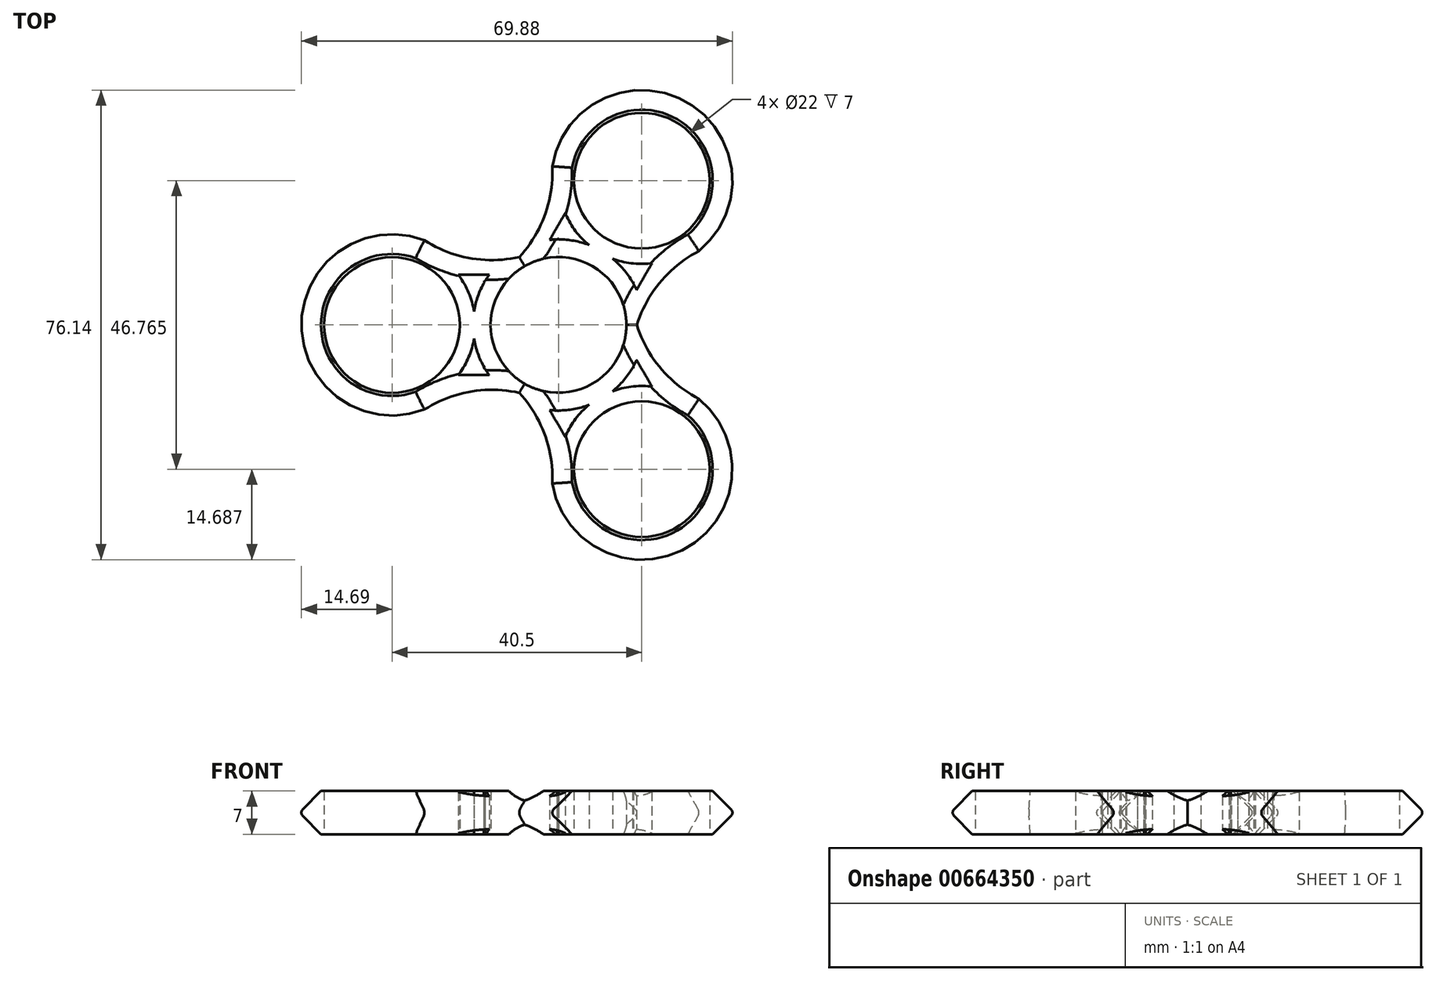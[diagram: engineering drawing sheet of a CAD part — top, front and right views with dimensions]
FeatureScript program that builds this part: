
annotation { "Feature Type Name" : "Feature", "Feature Type Description" : "" }
export const myFeature = defineFeature(function(context is Context, id is Id, definition is map)
    precondition{}
    {
        {
            var Q0;
            Q0=qCreatedBy(makeId("Front.planeOp"),FACE);
            var sketch = newSketch(context, id + "F0", { "sketchPlane" : qUnion([Q0])});
            skLineSegment(sketch, "E0", {"start": v(0, 0) * mm, "end": v(0, 6.18) * mm});
            skSolve(sketch);
        }
        {
            var Q0;
            Q0=qCreatedBy(makeId("Top.planeOp"),FACE);
            var sketch = newSketch(context, id + "F1", { "sketchPlane" : qUnion([Q0])});
            skArc(sketch, "E1", {"start": v(0, 11) * mm, "mid": v(-11, 0) * mm, "end": v(0, -11) * mm});
            skLineSegment(sketch, "E2", {"start": v(0, 56.07) * mm, "end": v(0, 11) * mm, "construction": true});
            skLineSegment(sketch, "E3", {"start": v(-42, 56.32) * mm, "end": v(-42, -55.95) * mm, "construction": true});
            skArc(sketch, "E4", {"start": v(-21.61, 14) * mm, "mid": v(-42, 0) * mm, "end": v(-21.61, -14) * mm});
            skLineSegment(sketch, "E5", {"start": v(0, 14) * mm, "end": v(0, 11) * mm});
            skLineSegment(sketch, "E6.trimOffspring", {"start": v(0, -11) * mm, "end": v(0, -55.82) * mm, "construction": true});
            skLineSegment(sketch, "E7.trimOffspring", {"start": v(0, -11) * mm, "end": v(0, -14) * mm});
            skCircle(sketch, "E8", {"center": v(-27, 0) * mm, "radius": 11 * mm});
            skArc(sketch, "E9", {"start": v(-21.61, 14) * mm, "mid": v(-10.8, 10.83) * mm, "end": v(0, 14) * mm});
            skArc(sketch, "E10", {"start": v(0, -14) * mm, "mid": v(-10.8, -10.83) * mm, "end": v(-21.61, -14) * mm});
            skArc(sketch, "E11", {"start": v(-16.24, -8.13) * mm, "mid": v(-14.6, -5.32) * mm, "end": v(-13.7, -2.2) * mm});
            skArc(sketch, "E12", {"start": v(-13.7, -2.2) * mm, "mid": v(-12.82, -5.3) * mm, "end": v(-11.24, -8.13) * mm});
            skLineSegment(sketch, "E13", {"start": v(-16.24, 8.13) * mm, "end": v(-11.24, 8.13) * mm});
            skLineSegment(sketch, "E14", {"start": v(-16.24, -8.13) * mm, "end": v(-11.24, -8.13) * mm});
            skArc(sketch, "E15.trimOffspring", {"start": v(-13.7, 2.2) * mm, "mid": v(-14.6, 5.32) * mm, "end": v(-16.24, 8.13) * mm});
            skArc(sketch, "E16.trimOffspring", {"start": v(-11.24, 8.13) * mm, "mid": v(-12.82, 5.3) * mm, "end": v(-13.7, 2.2) * mm});
            skArc(sketch, "E17.trimOffspring", {"start": v(0, 13.87) * mm, "mid": v(-0.1, 13.87) * mm, "end": v(-0.2, 13.87) * mm});
            skArc(sketch, "E18.trimOffspring", {"start": v(-0.2, -13.87) * mm, "mid": v(-0.1, -13.87) * mm, "end": v(0, -13.87) * mm});
            skSolve(sketch);
        }
        {
            var Q0;
            Q0=qSketchRegion(id+"F1",true);
            extrude(context, id + "F2", {"entities" : qUnion([Q0]), "depth" : 7 * mm, "offsetDistance" : 25 * mm});
        }
        {
            var Q0;
            Q0=makeQuery(id+"F2.opExtrude","SWEPT_BODY",BODY,{"disambiguationData":[OSD([sQuery(id+"F1.wireOp",EDGE,"E1"),sQuery(id+"F1.wireOp",EDGE,"E4"),sQuery(id+"F1.wireOp",EDGE,"FDauGuLe-8Zff-q5YO-oCp6-tykGBjxohg7e"),sQuery(id+"F1.wireOp",EDGE,"jIsLD8pJ-Ysfo-LJuf-yR93-SOJIJmbdSe7O"),sQuery(id+"F1.wireOp",EDGE,"E5"),sQuery(id+"F1.wireOp",EDGE,"E7.trimOffspring"),sQuery(id+"F1.wireOp",EDGE,"E8")])]});
            var Q1;
            Q1=sQuery(id+"F0.wireOp",EDGE,"E0");
            circularPattern(context, id + "F3", {"operationType" : NewBodyOperationType.ADD, "entities" : qUnion([Q0]), "axis" : qUnion([Q1]), "angle" : 240 * degree, "instanceCount" : 3, "equalSpace" : true});
        }
        {
            var Q0;
            {var subQ0=sQuery(id+"F1.wireOp",EDGE,"E10");var subQ2=sQuery(id+"F1.wireOp",EDGE,"E4");Q0=makeQuery(id+"F3.boolean.opBoolean","SPLIT",EDGE,{"disambiguationData":[TD([makeQuery(id+"F2.opExtrude","SWEPT_FACE",FACE,{"disambiguationData":[OSD([subQ2])]})])],"derivedFrom":makeQuery(id+"F2.opExtrude","CAP_EDGE",EDGE,{"disambiguationData":[OSD([subQ0])],"isStart":false})});}
            var Q1;
            {var subQ1=sQuery(id+"F1.wireOp",EDGE,"E10");var subQ2=sQuery(id+"F1.wireOp",EDGE,"E9");Q1=makeQuery(id+"F3.boolean.opBoolean","SPLIT",EDGE,{"disambiguationData":[TD([makeQuery(id+"F2.opExtrude","SWEPT_FACE",FACE,{"disambiguationData":[OSD([subQ1])]})])],"derivedFrom":makeQuery(id+"F3.opPattern","COPY",EDGE,{"derivedFrom":makeQuery(id+"F2.opExtrude","CAP_EDGE",EDGE,{"disambiguationData":[OSD([subQ2])],"isStart":false}),"instanceName":"1"})});}
            var Q2;
            Q2=makeQuery(id+"F3.opPattern","COPY",EDGE,{"derivedFrom":makeQuery(id+"F2.opExtrude","CAP_EDGE",EDGE,{"disambiguationData":[OSD([sQuery(id+"F1.wireOp",EDGE,"E4")])],"isStart":false}),"instanceName":"1"});
            var Q3;
            {var subQ0=sQuery(id+"F1.wireOp",EDGE,"E10");var subQ1=sQuery(id+"F1.wireOp",EDGE,"E4");Q3=makeQuery(id+"F3.boolean.opBoolean","SPLIT",EDGE,{"disambiguationData":[TD([makeQuery(id+"F3.opPattern","COPY",FACE,{"derivedFrom":makeQuery(id+"F2.opExtrude","SWEPT_FACE",FACE,{"disambiguationData":[OSD([subQ1])]}),"instanceName":"1"})])],"derivedFrom":makeQuery(id+"F3.opPattern","COPY",EDGE,{"derivedFrom":makeQuery(id+"F2.opExtrude","CAP_EDGE",EDGE,{"disambiguationData":[OSD([subQ0])],"isStart":false}),"instanceName":"1"})});}
            var Q4;
            {var subQ0=sQuery(id+"F1.wireOp",EDGE,"E10");var subQ1=sQuery(id+"F1.wireOp",EDGE,"E9");Q4=makeQuery(id+"F3.boolean.opBoolean","SPLIT",EDGE,{"disambiguationData":[TD([makeQuery(id+"F3.opPattern","COPY",FACE,{"derivedFrom":makeQuery(id+"F2.opExtrude","SWEPT_FACE",FACE,{"disambiguationData":[OSD([subQ0])]}),"instanceName":"1"})])],"derivedFrom":makeQuery(id+"F3.opPattern","COPY",EDGE,{"derivedFrom":makeQuery(id+"F2.opExtrude","CAP_EDGE",EDGE,{"disambiguationData":[OSD([subQ1])],"isStart":false}),"instanceName":"2"})});}
            var Q5;
            Q5=makeQuery(id+"F3.opPattern","COPY",EDGE,{"derivedFrom":makeQuery(id+"F2.opExtrude","CAP_EDGE",EDGE,{"disambiguationData":[OSD([sQuery(id+"F1.wireOp",EDGE,"E4")])],"isStart":false}),"instanceName":"2"});
            var Q6;
            {var subQ0=sQuery(id+"F1.wireOp",EDGE,"E10");var subQ1=sQuery(id+"F1.wireOp",EDGE,"E9");Q6=makeQuery(id+"F3.boolean.opBoolean","SPLIT",EDGE,{"disambiguationData":[TD([makeQuery(id+"F2.opExtrude","SWEPT_FACE",FACE,{"disambiguationData":[OSD([subQ1])]})])],"derivedFrom":makeQuery(id+"F3.opPattern","COPY",EDGE,{"derivedFrom":makeQuery(id+"F2.opExtrude","CAP_EDGE",EDGE,{"disambiguationData":[OSD([subQ0])],"isStart":false}),"instanceName":"2"})});}
            var Q7;
            {var subQ1=sQuery(id+"F1.wireOp",EDGE,"E9");var subQ2=sQuery(id+"F1.wireOp",EDGE,"E4");Q7=makeQuery(id+"F3.boolean.opBoolean","SPLIT",EDGE,{"disambiguationData":[TD([makeQuery(id+"F2.opExtrude","SWEPT_FACE",FACE,{"disambiguationData":[OSD([subQ2])]})])],"derivedFrom":makeQuery(id+"F2.opExtrude","CAP_EDGE",EDGE,{"disambiguationData":[OSD([subQ1])],"isStart":false})});}
            var Q8;
            Q8=makeQuery(id+"F2.opExtrude","CAP_EDGE",EDGE,{"disambiguationData":[OSD([sQuery(id+"F1.wireOp",EDGE,"E4")])],"isStart":false});
            var Q9;
            Q9=makeQuery(id+"F2.opExtrude","CAP_EDGE",EDGE,{"disambiguationData":[OSD([sQuery(id+"F1.wireOp",EDGE,"E4")])],"isStart":true});
            var Q10;
            {var subQ0=sQuery(id+"F1.wireOp",EDGE,"E10");var subQ2=sQuery(id+"F1.wireOp",EDGE,"E4");Q10=makeQuery(id+"F3.boolean.opBoolean","SPLIT",EDGE,{"disambiguationData":[TD([makeQuery(id+"F2.opExtrude","SWEPT_FACE",FACE,{"disambiguationData":[OSD([subQ2])]})])],"derivedFrom":makeQuery(id+"F2.opExtrude","CAP_EDGE",EDGE,{"disambiguationData":[OSD([subQ0])],"isStart":true})});}
            var Q11;
            {var subQ1=sQuery(id+"F1.wireOp",EDGE,"E10");var subQ2=sQuery(id+"F1.wireOp",EDGE,"E9");Q11=makeQuery(id+"F3.boolean.opBoolean","SPLIT",EDGE,{"disambiguationData":[TD([makeQuery(id+"F2.opExtrude","SWEPT_FACE",FACE,{"disambiguationData":[OSD([subQ1])]})])],"derivedFrom":makeQuery(id+"F3.opPattern","COPY",EDGE,{"derivedFrom":makeQuery(id+"F2.opExtrude","CAP_EDGE",EDGE,{"disambiguationData":[OSD([subQ2])],"isStart":true}),"instanceName":"1"})});}
            var Q12;
            Q12=makeQuery(id+"F3.opPattern","COPY",EDGE,{"derivedFrom":makeQuery(id+"F2.opExtrude","CAP_EDGE",EDGE,{"disambiguationData":[OSD([sQuery(id+"F1.wireOp",EDGE,"E4")])],"isStart":true}),"instanceName":"1"});
            var Q13;
            {var subQ0=sQuery(id+"F1.wireOp",EDGE,"E10");var subQ2=sQuery(id+"F1.wireOp",EDGE,"E4");Q13=makeQuery(id+"F3.boolean.opBoolean","SPLIT",EDGE,{"disambiguationData":[TD([makeQuery(id+"F3.opPattern","COPY",FACE,{"derivedFrom":makeQuery(id+"F2.opExtrude","SWEPT_FACE",FACE,{"disambiguationData":[OSD([subQ2])]}),"instanceName":"1"})])],"derivedFrom":makeQuery(id+"F3.opPattern","COPY",EDGE,{"derivedFrom":makeQuery(id+"F2.opExtrude","CAP_EDGE",EDGE,{"disambiguationData":[OSD([subQ0])],"isStart":true}),"instanceName":"1"})});}
            var Q14;
            {var subQ0=sQuery(id+"F1.wireOp",EDGE,"E10");var subQ1=sQuery(id+"F1.wireOp",EDGE,"E9");Q14=makeQuery(id+"F3.boolean.opBoolean","SPLIT",EDGE,{"disambiguationData":[TD([makeQuery(id+"F3.opPattern","COPY",FACE,{"derivedFrom":makeQuery(id+"F2.opExtrude","SWEPT_FACE",FACE,{"disambiguationData":[OSD([subQ0])]}),"instanceName":"1"})])],"derivedFrom":makeQuery(id+"F3.opPattern","COPY",EDGE,{"derivedFrom":makeQuery(id+"F2.opExtrude","CAP_EDGE",EDGE,{"disambiguationData":[OSD([subQ1])],"isStart":true}),"instanceName":"2"})});}
            var Q15;
            Q15=makeQuery(id+"F3.opPattern","COPY",EDGE,{"derivedFrom":makeQuery(id+"F2.opExtrude","CAP_EDGE",EDGE,{"disambiguationData":[OSD([sQuery(id+"F1.wireOp",EDGE,"E4")])],"isStart":true}),"instanceName":"2"});
            var Q16;
            {var subQ0=sQuery(id+"F1.wireOp",EDGE,"E10");var subQ1=sQuery(id+"F1.wireOp",EDGE,"E9");Q16=makeQuery(id+"F3.boolean.opBoolean","SPLIT",EDGE,{"disambiguationData":[TD([makeQuery(id+"F2.opExtrude","SWEPT_FACE",FACE,{"disambiguationData":[OSD([subQ1])]})])],"derivedFrom":makeQuery(id+"F3.opPattern","COPY",EDGE,{"derivedFrom":makeQuery(id+"F2.opExtrude","CAP_EDGE",EDGE,{"disambiguationData":[OSD([subQ0])],"isStart":true}),"instanceName":"2"})});}
            var Q17;
            {var subQ1=sQuery(id+"F1.wireOp",EDGE,"E9");var subQ2=sQuery(id+"F1.wireOp",EDGE,"E4");Q17=makeQuery(id+"F3.boolean.opBoolean","SPLIT",EDGE,{"disambiguationData":[TD([makeQuery(id+"F2.opExtrude","SWEPT_FACE",FACE,{"disambiguationData":[OSD([subQ2])]})])],"derivedFrom":makeQuery(id+"F2.opExtrude","CAP_EDGE",EDGE,{"disambiguationData":[OSD([subQ1])],"isStart":true})});}
            chamfer(context, id + "F4", {"entities" : qUnion([Q0, Q1, Q2, Q3, Q4, Q5, Q6, Q7, Q8, Q9, Q10, Q11, Q12, Q13, Q14, Q15, Q16, Q17]), "width" : 3.5 * mm, "tangentPropagation" : true});
        }
        {
            var Q0;
            {var subQ0=sQuery(id+"F1.wireOp",EDGE,"E4");Q0=makeQuery(id+"F4.opChamfer","BLEND_EDGE",EDGE,{"blendedFrom":[makeQuery(id+"F3.opPattern","COPY",EDGE,{"derivedFrom":makeQuery(id+"F2.opExtrude","CAP_EDGE",EDGE,{"disambiguationData":[OSD([subQ0])],"isStart":true}),"instanceName":"1"}),makeQuery(id+"F3.opPattern","COPY",EDGE,{"derivedFrom":makeQuery(id+"F2.opExtrude","CAP_EDGE",EDGE,{"disambiguationData":[OSD([subQ0])],"isStart":false}),"instanceName":"1"})],"blendedInto":[]});}
            var Q1;
            {var subQ0=sQuery(id+"F1.wireOp",EDGE,"E10");var subQ2=sQuery(id+"F1.wireOp",EDGE,"E4");var subQ3=makeQuery(id+"F3.opPattern","COPY",FACE,{"derivedFrom":makeQuery(id+"F2.opExtrude","SWEPT_FACE",FACE,{"disambiguationData":[OSD([subQ2])]}),"instanceName":"1"});Q1=makeQuery(id+"F4.opChamfer","BLEND_EDGE",EDGE,{"blendedFrom":[makeQuery(id+"F3.boolean.opBoolean","SPLIT",EDGE,{"disambiguationData":[TD([subQ3])],"derivedFrom":makeQuery(id+"F3.opPattern","COPY",EDGE,{"derivedFrom":makeQuery(id+"F2.opExtrude","CAP_EDGE",EDGE,{"disambiguationData":[OSD([subQ0])],"isStart":true}),"instanceName":"1"})}),makeQuery(id+"F3.boolean.opBoolean","SPLIT",EDGE,{"disambiguationData":[TD([subQ3])],"derivedFrom":makeQuery(id+"F3.opPattern","COPY",EDGE,{"derivedFrom":makeQuery(id+"F2.opExtrude","CAP_EDGE",EDGE,{"disambiguationData":[OSD([subQ0])],"isStart":false}),"instanceName":"1"})})],"blendedInto":[]});}
            var Q2;
            {var subQ0=sQuery(id+"F1.wireOp",EDGE,"E10");var subQ1=makeQuery(id+"F3.opPattern","COPY",FACE,{"derivedFrom":makeQuery(id+"F2.opExtrude","SWEPT_FACE",FACE,{"disambiguationData":[OSD([subQ0])]}),"instanceName":"1"});var subQ8=sQuery(id+"F1.wireOp",EDGE,"E9");Q2=makeQuery(id+"F4.opChamfer","BLEND_EDGE",EDGE,{"blendedFrom":[makeQuery(id+"F3.boolean.opBoolean","SPLIT",EDGE,{"disambiguationData":[TD([subQ1])],"derivedFrom":makeQuery(id+"F3.opPattern","COPY",EDGE,{"derivedFrom":makeQuery(id+"F2.opExtrude","CAP_EDGE",EDGE,{"disambiguationData":[OSD([subQ8])],"isStart":true}),"instanceName":"2"})}),makeQuery(id+"F3.boolean.opBoolean","SPLIT",EDGE,{"disambiguationData":[TD([subQ1])],"derivedFrom":makeQuery(id+"F3.opPattern","COPY",EDGE,{"derivedFrom":makeQuery(id+"F2.opExtrude","CAP_EDGE",EDGE,{"disambiguationData":[OSD([subQ8])],"isStart":false}),"instanceName":"2"})})],"blendedInto":[]});}
            var Q3;
            {var subQ0=sQuery(id+"F1.wireOp",EDGE,"E4");Q3=makeQuery(id+"F4.opChamfer","BLEND_EDGE",EDGE,{"blendedFrom":[makeQuery(id+"F3.opPattern","COPY",EDGE,{"derivedFrom":makeQuery(id+"F2.opExtrude","CAP_EDGE",EDGE,{"disambiguationData":[OSD([subQ0])],"isStart":true}),"instanceName":"2"}),makeQuery(id+"F3.opPattern","COPY",EDGE,{"derivedFrom":makeQuery(id+"F2.opExtrude","CAP_EDGE",EDGE,{"disambiguationData":[OSD([subQ0])],"isStart":false}),"instanceName":"2"})],"blendedInto":[]});}
            var Q4;
            {var subQ6=sQuery(id+"F1.wireOp",EDGE,"E10");var subQ7=sQuery(id+"F1.wireOp",EDGE,"E9");var subQ14=makeQuery(id+"F2.opExtrude","SWEPT_FACE",FACE,{"disambiguationData":[OSD([subQ7])]});Q4=makeQuery(id+"F4.opChamfer","BLEND_EDGE",EDGE,{"blendedFrom":[makeQuery(id+"F3.boolean.opBoolean","SPLIT",EDGE,{"disambiguationData":[TD([subQ14])],"derivedFrom":makeQuery(id+"F3.opPattern","COPY",EDGE,{"derivedFrom":makeQuery(id+"F2.opExtrude","CAP_EDGE",EDGE,{"disambiguationData":[OSD([subQ6])],"isStart":true}),"instanceName":"2"})}),makeQuery(id+"F3.boolean.opBoolean","SPLIT",EDGE,{"disambiguationData":[TD([subQ14])],"derivedFrom":makeQuery(id+"F3.opPattern","COPY",EDGE,{"derivedFrom":makeQuery(id+"F2.opExtrude","CAP_EDGE",EDGE,{"disambiguationData":[OSD([subQ6])],"isStart":false}),"instanceName":"2"})})],"blendedInto":[]});}
            var Q5;
            {var subQ7=sQuery(id+"F1.wireOp",EDGE,"E9");var subQ11=sQuery(id+"F1.wireOp",EDGE,"E4");var subQ14=makeQuery(id+"F2.opExtrude","SWEPT_FACE",FACE,{"disambiguationData":[OSD([subQ11])]});Q5=makeQuery(id+"F4.opChamfer","BLEND_EDGE",EDGE,{"blendedFrom":[makeQuery(id+"F3.boolean.opBoolean","SPLIT",EDGE,{"disambiguationData":[TD([subQ14])],"derivedFrom":makeQuery(id+"F2.opExtrude","CAP_EDGE",EDGE,{"disambiguationData":[OSD([subQ7])],"isStart":true})}),makeQuery(id+"F3.boolean.opBoolean","SPLIT",EDGE,{"disambiguationData":[TD([subQ14])],"derivedFrom":makeQuery(id+"F2.opExtrude","CAP_EDGE",EDGE,{"disambiguationData":[OSD([subQ7])],"isStart":false})})],"blendedInto":[]});}
            var Q6;
            {var subQ0=sQuery(id+"F1.wireOp",EDGE,"E4");Q6=makeQuery(id+"F4.opChamfer","BLEND_EDGE",EDGE,{"blendedFrom":[makeQuery(id+"F2.opExtrude","CAP_EDGE",EDGE,{"disambiguationData":[OSD([subQ0])],"isStart":true}),makeQuery(id+"F2.opExtrude","CAP_EDGE",EDGE,{"disambiguationData":[OSD([subQ0])],"isStart":false})],"blendedInto":[]});}
            var Q7;
            {var subQ6=sQuery(id+"F1.wireOp",EDGE,"E10");var subQ11=sQuery(id+"F1.wireOp",EDGE,"E4");var subQ15=makeQuery(id+"F2.opExtrude","SWEPT_FACE",FACE,{"disambiguationData":[OSD([subQ11])]});Q7=makeQuery(id+"F4.opChamfer","BLEND_EDGE",EDGE,{"blendedFrom":[makeQuery(id+"F3.boolean.opBoolean","SPLIT",EDGE,{"disambiguationData":[TD([subQ15])],"derivedFrom":makeQuery(id+"F2.opExtrude","CAP_EDGE",EDGE,{"disambiguationData":[OSD([subQ6])],"isStart":true})}),makeQuery(id+"F3.boolean.opBoolean","SPLIT",EDGE,{"disambiguationData":[TD([subQ15])],"derivedFrom":makeQuery(id+"F2.opExtrude","CAP_EDGE",EDGE,{"disambiguationData":[OSD([subQ6])],"isStart":false})})],"blendedInto":[]});}
            var Q8;
            {var subQ8=sQuery(id+"F1.wireOp",EDGE,"E10");var subQ9=sQuery(id+"F1.wireOp",EDGE,"E9");var subQ15=makeQuery(id+"F2.opExtrude","SWEPT_FACE",FACE,{"disambiguationData":[OSD([subQ8])]});Q8=makeQuery(id+"F4.opChamfer","BLEND_EDGE",EDGE,{"blendedFrom":[makeQuery(id+"F3.boolean.opBoolean","SPLIT",EDGE,{"disambiguationData":[TD([subQ15])],"derivedFrom":makeQuery(id+"F3.opPattern","COPY",EDGE,{"derivedFrom":makeQuery(id+"F2.opExtrude","CAP_EDGE",EDGE,{"disambiguationData":[OSD([subQ9])],"isStart":true}),"instanceName":"1"})}),makeQuery(id+"F3.boolean.opBoolean","SPLIT",EDGE,{"disambiguationData":[TD([subQ15])],"derivedFrom":makeQuery(id+"F3.opPattern","COPY",EDGE,{"derivedFrom":makeQuery(id+"F2.opExtrude","CAP_EDGE",EDGE,{"disambiguationData":[OSD([subQ9])],"isStart":false}),"instanceName":"1"})})],"blendedInto":[]});}
            fillet(context, id + "F5", {"entities" : qUnion([Q0, Q1, Q2, Q3, Q4, Q5, Q6, Q7, Q8]), "radius" : .75 * mm, "tangentPropagation" : true, "allowEdgeOverflow" : false});
        }
    });
